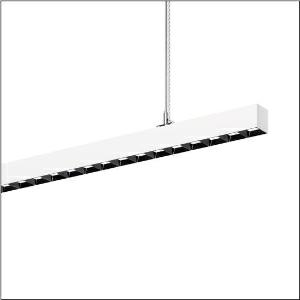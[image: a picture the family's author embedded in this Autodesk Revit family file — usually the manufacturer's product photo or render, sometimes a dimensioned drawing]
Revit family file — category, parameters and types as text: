
# Revit family: silica_r__21_51mx31tat7w_6f20
name_source: partatom
category: Lighting Fixtures
units: mm (PartAtom-declared; Revit-internal decimal feet)

## family parameters
Cut with Voids When Loaded = No
Host = Face
Light Source = No
Part Type = Normal
Room Calculation Point = No
Round Connector Dimension = Use Diameter
Shared = No

## types (1)
- --- (1 x LED, 6220 lm, 53.5 W, 6500K)
    Apparent Load = 54 VA
    CIE Flux Codes = 85 99 100 60 100
    Color Rendering = 80
    Color Temperature = 6500K
    Default Elevation = 1800 mm
    Description = Silica® 21, office luminaire, primary light control with darklight reflector, of PMMA, black, CAT 2 (L<= 3000cd/m²), light emission: direct/indirect distribution, primary light characteristic: symmetric, installation type: suspended mounting, LED, rated luminous flux: 6.220lm, luminous efficacy: 111lm/W, light colour: 8tw, colour temperature: 2700..6500K, control gear: ECG DALI, with terminal, 3+2-pole, max. 2.5mm², mains connection: 220..240V, AC, 50/60Hz, rated input power: 56.2W, luminaire housing, of aluminium, traffic white (RAL 9016), length: 1.204mm, width: 53mm, height: 53mm, protection rating (complete): IP20, insulation class (complete): insulation class I (protective earthing), certification: CE, permissible operating ambient temperature: 0..+35°C, standard: EN 50419, packaging unit: 1 piece
    Height = 53 mm
    Lamp = 1 x LED
    Lamp Light Flux = 6220 lm
    Lamp Power = 53.5 W
    Lamp count = 1
    Length = 1204 mm
    Luminous efficacy = 116 lm/W
    Manufacturer = Siteco
    ModVariant = No
    Model = 51MX31TAT7W
    Mounting Place = Ceiling
    Mounting Type = Pendant
    Number of Poles = 1
    OnlyDefault = Yes
    Power Factor = 1
    Product Name = Silica® 21
    Product group = office luminaire | ceiling pendant
    ProductGroupID = 902
    Protection Class = Protection class I
    Protection Degree = IP 20
    RLX_Detail_Level = 1
    RLX_Emergency_Light_Flux = 0 lm
    RLX_Emergency_Type = 0
    RLX_Emergency_Type_DB = No
    RlxData = <blob elided: 40365 chars, md5=a0a4e2c1>
    Socket = socket
    Standby Power = 0 W
    System Light Flux = 6220 lm
    System Power = 54 W
    Type Comments = individual setting
    Type Image = l_1335871.jpg
    URL = http://relux.com
    VarID = @adj_109711
    Voltage = 0 V
    Weight = 0.00 kg
    Width = 53 mm

## geometry (parser evidence)
native form markers: Blend x4, Sweep x10
no freeform markers — native parametric forms only
